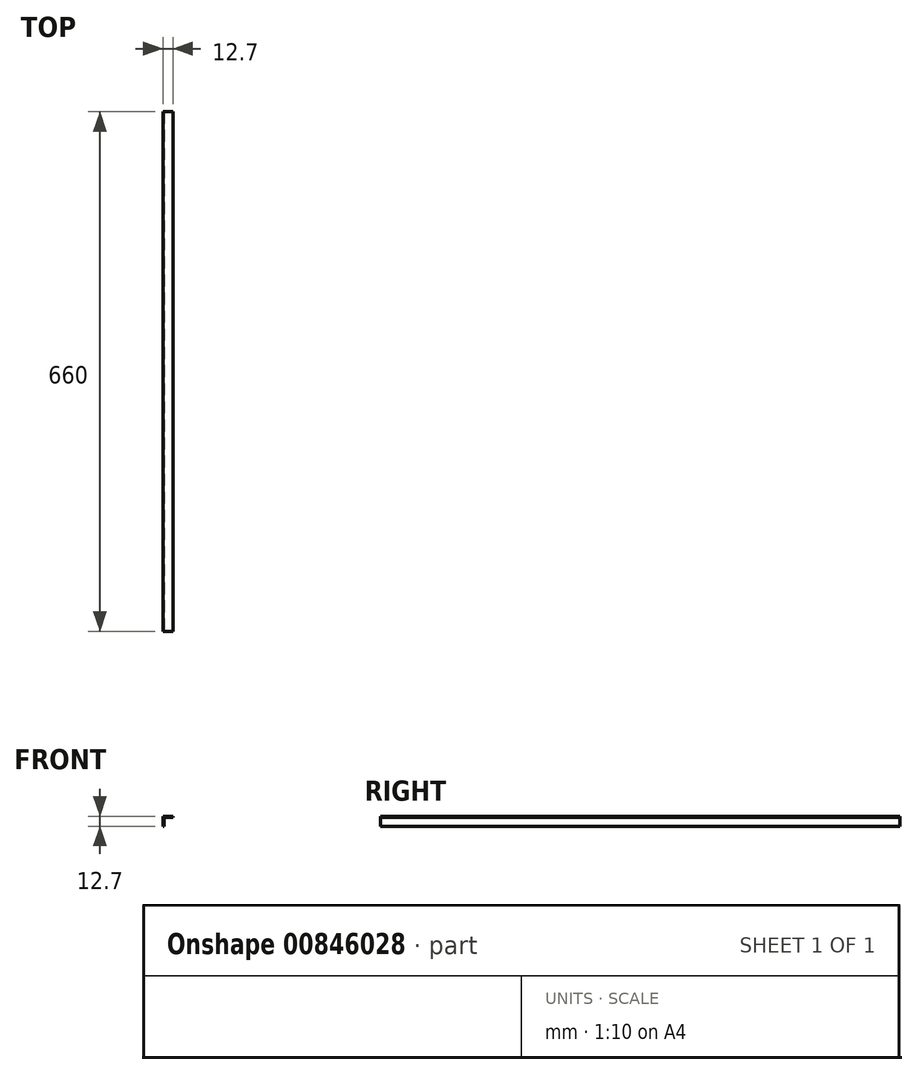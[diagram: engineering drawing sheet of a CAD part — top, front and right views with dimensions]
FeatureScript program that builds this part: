
annotation { "Feature Type Name" : "Feature", "Feature Type Description" : "" }
export const myFeature = defineFeature(function(context is Context, id is Id, definition is map)
    precondition{}
    {
        {
            var Q0;
            Q0=qCreatedBy(makeId("Front.planeOp"),FACE);
            var sketch = newSketch(context, id + "F0", { "sketchPlane" : qUnion([Q0])});
            skLineSegment(sketch, "E0", {"start": v(-6.35, 0) * mm, "end": v(-6.35, -12.7) * mm});
            skLineSegment(sketch, "E1", {"start": v(-6.35, -12.7) * mm, "end": v(-4.76, -12.7) * mm});
            skLineSegment(sketch, "E2", {"start": v(-4.76, -12.7) * mm, "end": v(-4.76, -1.59) * mm});
            skLineSegment(sketch, "E3", {"start": v(-4.76, -1.59) * mm, "end": v(6.35, -1.59) * mm});
            skLineSegment(sketch, "E4", {"start": v(6.35, -1.59) * mm, "end": v(6.35, 0) * mm});
            skLineSegment(sketch, "E5", {"start": v(6.35, 0) * mm, "end": v(-6.35, 0) * mm});
            skSolve(sketch);
        }
        {
            var Q0;
            Q0 = qSketchRegion(id + "F0", true);
            extrude(context, id + "F1", {"entities" : qUnion([Q0]), "oppositeDirection" : true, "depth" : 660 * mm, "offsetDistance" : 25.4 * mm});
        }
    });
